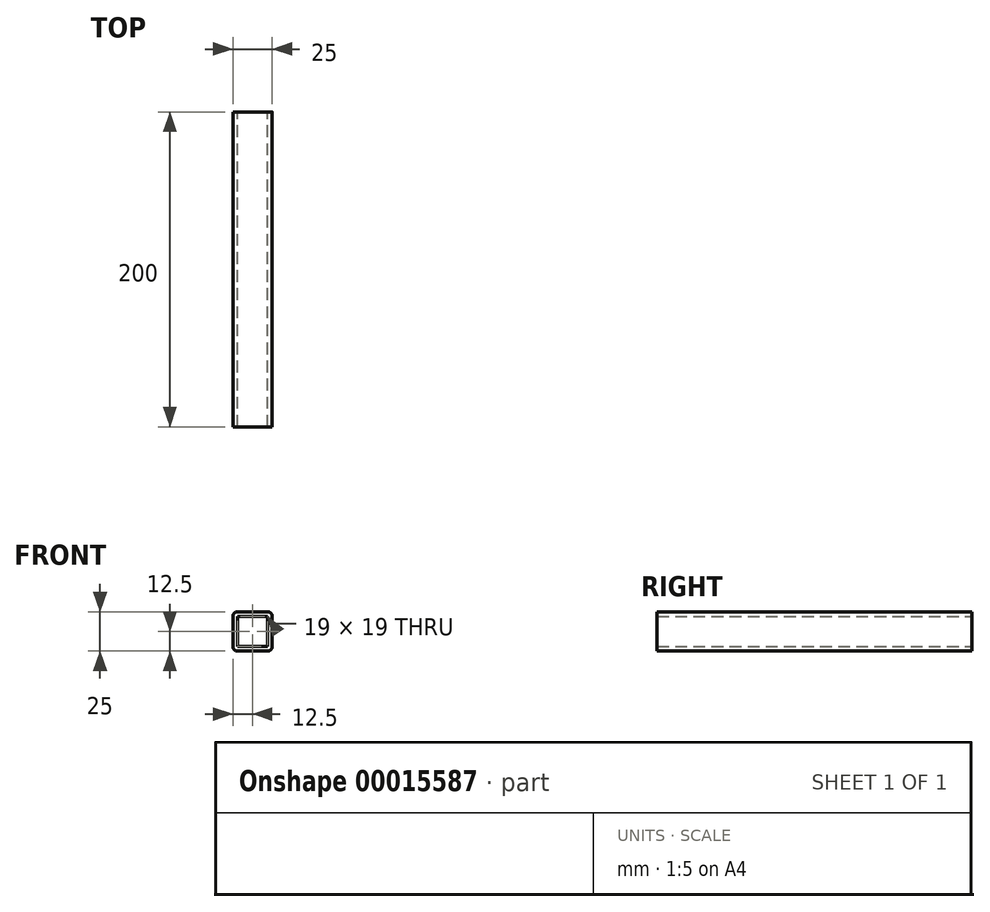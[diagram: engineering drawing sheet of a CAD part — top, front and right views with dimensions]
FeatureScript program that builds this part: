
annotation { "Feature Type Name" : "Feature", "Feature Type Description" : "" }
export const myFeature = defineFeature(function(context is Context, id is Id, definition is map)
    precondition{}
    {
        {
            var Q0;
            Q0=qCreatedBy(makeId("Front.planeOp"),FACE);
            var sketch = newSketch(context, id + "F0", { "sketchPlane" : qUnion([Q0])});
            skLineSegment(sketch, "E0.bottom", {"start": v(3, 0) * mm, "end": v(22, 0) * mm});
            skLineSegment(sketch, "E0.top", {"start": v(3, 25) * mm, "end": v(22, 25) * mm});
            skLineSegment(sketch, "E0.left", {"start": v(0, 3) * mm, "end": v(0, 22) * mm});
            skLineSegment(sketch, "E0.right", {"start": v(25, 3) * mm, "end": v(25, 22) * mm});
            skLineSegment(sketch, "E1.0", {"start": v(3, 22) * mm, "end": v(22, 22) * mm});
            skLineSegment(sketch, "E1.1", {"start": v(3, 3) * mm, "end": v(3, 22) * mm});
            skLineSegment(sketch, "E1.2", {"start": v(3, 3) * mm, "end": v(22, 3) * mm});
            skLineSegment(sketch, "E1.3", {"start": v(22, 3) * mm, "end": v(22, 22) * mm});
            skPoint(sketch, "E2.visualSharp", {"position": v(0, 25) * mm});
            skArc(sketch, "E2.filletArc", {"start": v(3, 25) * mm, "mid": v(0.88, 24.12) * mm, "end": v(0, 22) * mm});
            skPoint(sketch, "E3.visualSharp", {"position": v(0, 0) * mm});
            skArc(sketch, "E3.filletArc", {"start": v(0, 3) * mm, "mid": v(0.88, 0.88) * mm, "end": v(3, 0) * mm});
            skPoint(sketch, "E4.visualSharp", {"position": v(25, 0) * mm});
            skArc(sketch, "E4.filletArc", {"start": v(22, 0) * mm, "mid": v(24.12, 0.88) * mm, "end": v(25, 3) * mm});
            skPoint(sketch, "E5.visualSharp", {"position": v(25, 25) * mm});
            skArc(sketch, "E5.filletArc", {"start": v(25, 22) * mm, "mid": v(24.12, 24.12) * mm, "end": v(22, 25) * mm});
            skSolve(sketch);
        }
        {
            var Q0;
            Q0=makeQuery(id+"F0.imprint","IMPRINT",FACE,{"disambiguationData":[TD([[makeQuery(id+"F0.imprint","IMPRINT",EDGE,{"derivedFrom":sQuery(id+"F0.wireOp",EDGE,"E0.bottom")}),1.0]])]});
            extrude(context, id + "F1", {"entities" : qUnion([Q0]), "depth" : 200 * mm});
        }
    });
